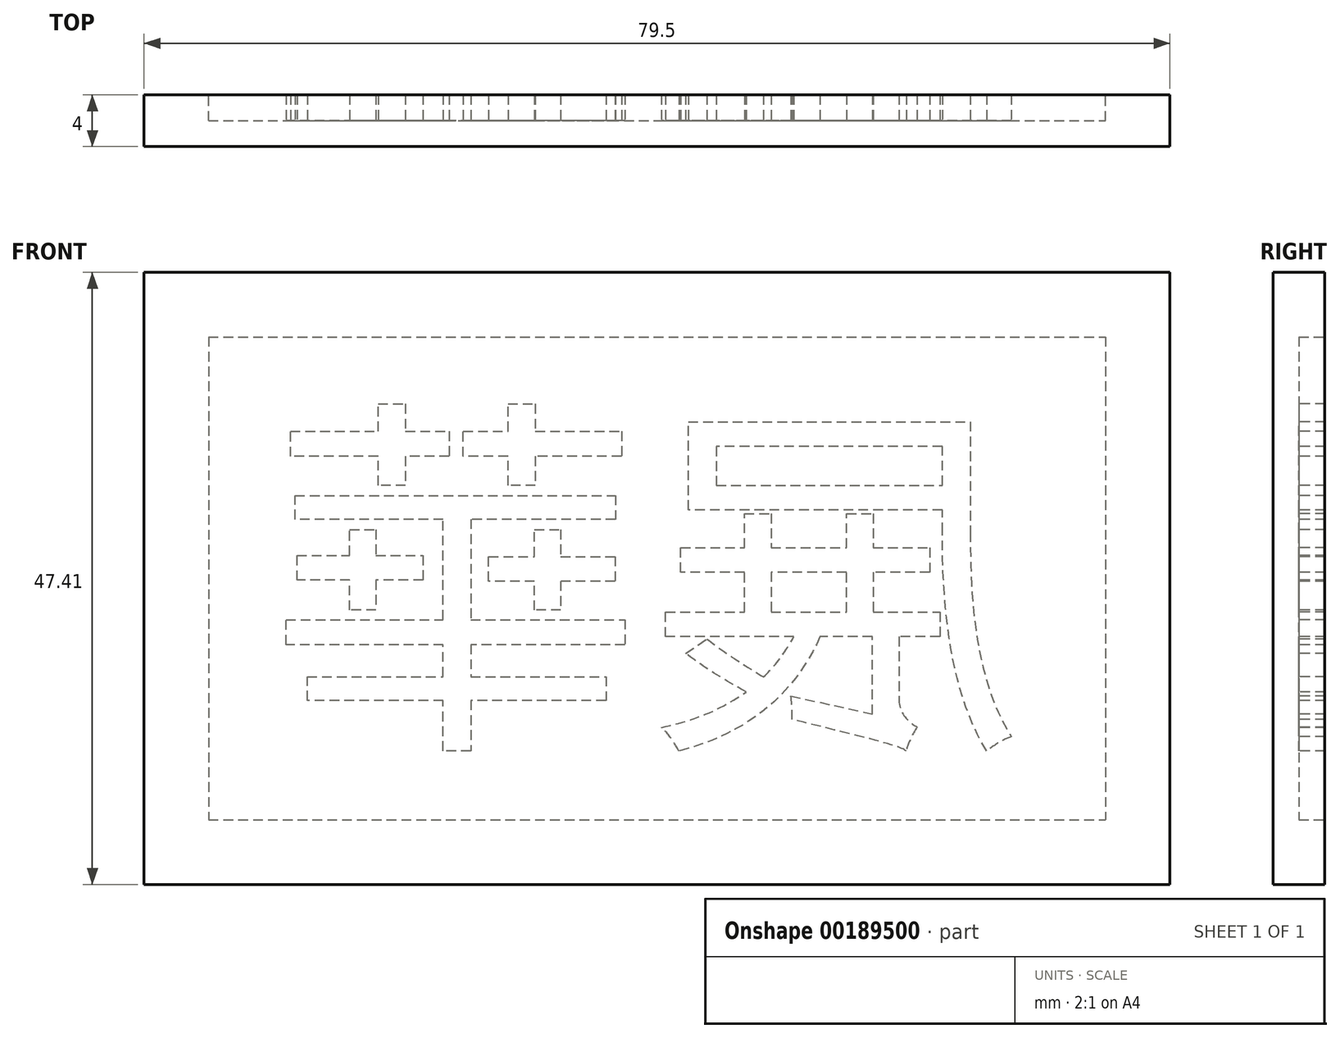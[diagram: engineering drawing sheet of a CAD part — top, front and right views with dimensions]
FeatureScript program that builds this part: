
annotation { "Feature Type Name" : "Feature", "Feature Type Description" : "" }
export const myFeature = defineFeature(function(context is Context, id is Id, definition is map)
    precondition{}
    {
        {
            var Q0;
            Q0=qCreatedBy(makeId("Front.planeOp"),FACE);
            var sketch = newSketch(context, id + "F0", { "sketchPlane" : qUnion([Q0])});
            skLineSegment(sketch, "E0.bottom", {"start": v(-36.47, 29.72) * mm, "end": v(43.03, 29.72) * mm});
            skLineSegment(sketch, "E0.top", {"start": v(-36.47, -17.69) * mm, "end": v(43.03, -17.69) * mm});
            skLineSegment(sketch, "E0.left", {"start": v(-36.47, 29.72) * mm, "end": v(-36.47, -17.69) * mm});
            skLineSegment(sketch, "E0.right", {"start": v(43.03, 29.72) * mm, "end": v(43.03, -17.69) * mm});
            skSolve(sketch);
        }
        {
            var Q0;
            Q0=qCreatedBy(makeId("Front.planeOp"),FACE);
            var sketch = newSketch(context, id + "F1", { "sketchPlane" : qUnion([Q0])});
            skLineSegment(sketch, "E1.0", {"start": v(-31.47, 24.72) * mm, "end": v(38.03, 24.72) * mm});
            skLineSegment(sketch, "E1.1", {"start": v(-31.47, 24.72) * mm, "end": v(-31.47, -12.69) * mm});
            skLineSegment(sketch, "E1.2", {"start": v(-31.47, -12.69) * mm, "end": v(38.03, -12.69) * mm});
            skLineSegment(sketch, "E1.3", {"start": v(38.03, 24.72) * mm, "end": v(38.03, -12.69) * mm});
            skSolve(sketch);
        }
        {
            var Q0;
            Q0 = qSketchRegion(id + "F0", true);
            extrude(context, id + "F2", {"entities" : qUnion([Q0]), "depth" : 4 * mm});
        }
        {
            var Q0;
            Q0 = qSketchRegion(id + "F1", true);
            extrude(context, id + "F3", {"entities" : qUnion([Q0]), "operationType" : NewBodyOperationType.REMOVE, "depth" : 2 * mm});
        }
        {
            var Q0;
            Q0=makeQuery(id+"F3.boolean.opBoolean","COPY",FACE,{"derivedFrom":makeQuery(id+"F3.opExtrude","CAP_FACE",FACE,{"disambiguationData":[OSD([sQuery(id+"F1.wireOp",EDGE,"E1.0"),sQuery(id+"F1.wireOp",EDGE,"E1.1"),sQuery(id+"F1.wireOp",EDGE,"E1.2"),sQuery(id+"F1.wireOp",EDGE,"E1.3")])],"isStart":false})});
            var sketch = newSketch(context, id + "F4", { "sketchPlane" : qUnion([Q0])});
            skText(sketch, "E2", { "text": "展華", "fontName": "NotoSansCJKtc-Regular.otf"});
            const initialGuessF4  = {"E2": [-0.0318, -0.00506, 1, 0, 0.02118]};
            skSetInitialGuess(sketch, initialGuessF4);
            skSolve(sketch);
        }
        {
            var Q0;
            Q0 = qSketchRegion(id + "F4", true);
            extrude(context, id + "F5", {"entities" : qUnion([Q0]), "operationType" : NewBodyOperationType.ADD, "depth" : 2 * mm});
        }
    });
